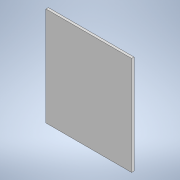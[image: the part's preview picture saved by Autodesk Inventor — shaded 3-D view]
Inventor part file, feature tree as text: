
AUTODESK INVENTOR PART (.ipt)
format: ipt  version: 2021 (Build 250183000, 183)  size: 91,136 bytes
history: native  units: mm
features: extrude x1, sketch x1
ambient origin geometry x8: Origin, YZ Plane, XZ Plane, XY Plane, X Axis, Y Axis, Z Axis, Center Point
bodies: Solid1 (feature_tree)
feature tree (2):
  extrude  "Extrusion1"  Depth=81.6mm
  sketch  "Sketch1"  dims[d0=70.8mm d1=81.6mm d2=2.0mm d3=0.0mm d8=0.5mm d9=0.872665mm d10=0.5mm d11=0.872665mm]
